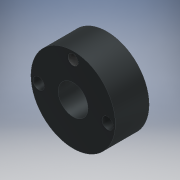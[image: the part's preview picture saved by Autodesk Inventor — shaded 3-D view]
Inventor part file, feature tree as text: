
AUTODESK INVENTOR PART (.ipt)
format: ipt  version: 2018 (Build 220112000, 112)  size: 137,216 bytes
history: native  units: mm
features: sketch x4, extrude x2, hole x2
ambient origin geometry x8: Origin, YZ Plane, XZ Plane, XY Plane, X Axis, Y Axis, Z Axis, Center Point
bodies: Solido1 (feature_tree)
feature tree (8):
  extrude  "Estrusione1"  Depth=30.0mm
  extrude  "Estrusione2"  Depth=80.0mm
  hole  "Foro1"  [1 undecoded]
  hole  "Foro2"  [1 undecoded]
  sketch  "Schizzo1"
  sketch  "Schizzo2"
  sketch  "Schizzo3"
  sketch  "Schizzo4"
note: 2 required parameter values undecoded (feature->parameter linkage not recoverable at this tier; creation-order binding heuristic only, values carry confidence <= 0.55)
